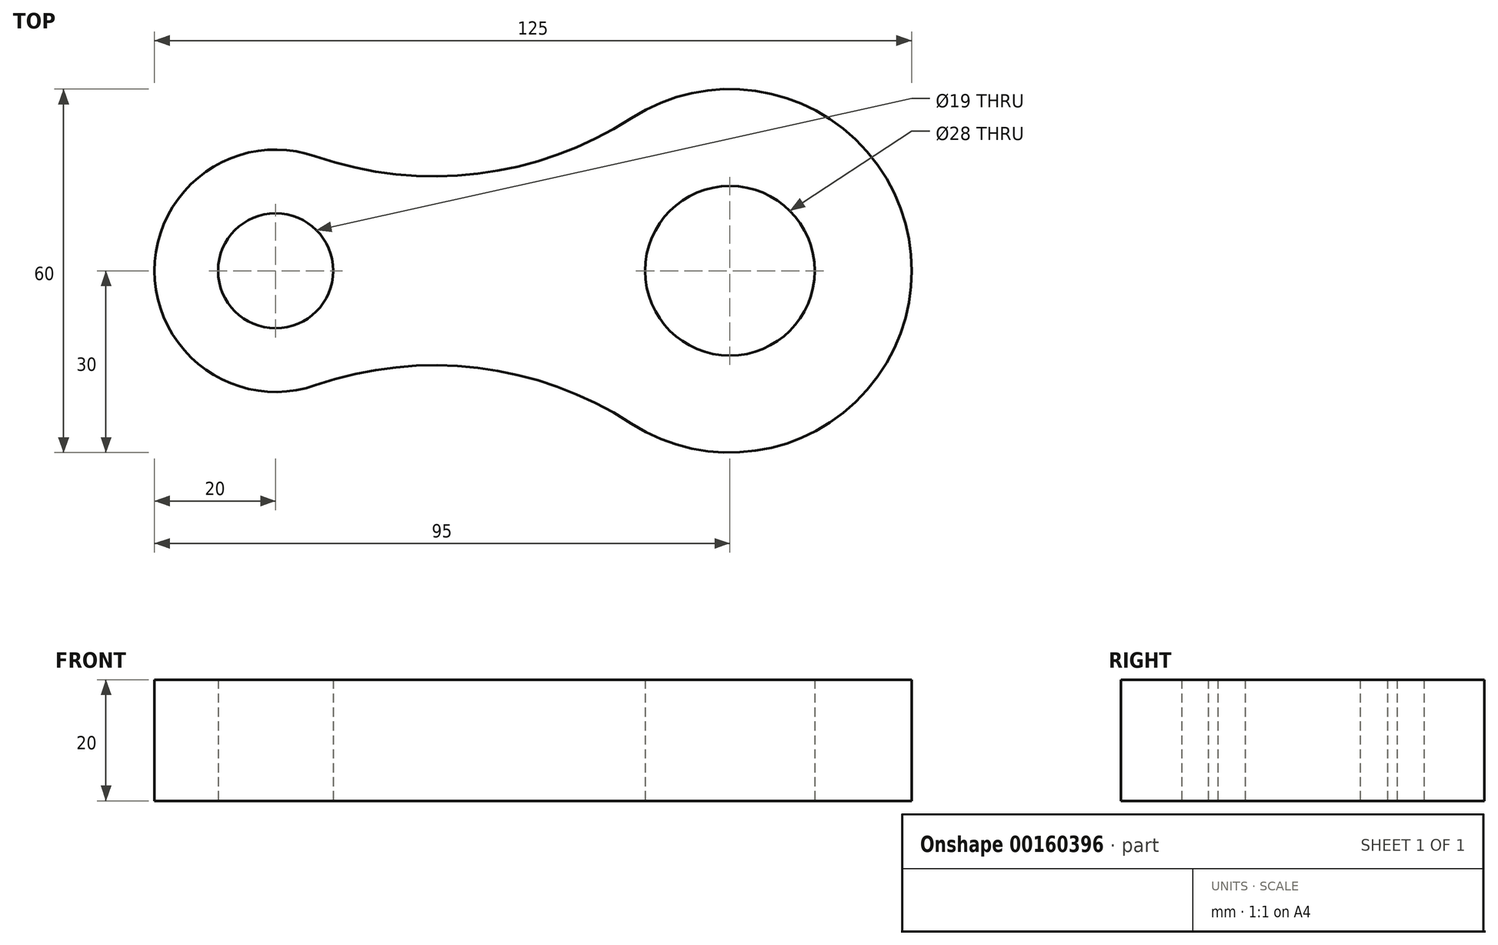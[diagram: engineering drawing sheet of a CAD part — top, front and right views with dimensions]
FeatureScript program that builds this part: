
annotation { "Feature Type Name" : "Feature", "Feature Type Description" : "" }
export const myFeature = defineFeature(function(context is Context, id is Id, definition is map)
    precondition{}
    {
        {
            var Q0;
            Q0=qCreatedBy(makeId("Top.planeOp"),FACE);
            var sketch = newSketch(context, id + "F0", { "sketchPlane" : qUnion([Q0])});
            skCircle(sketch, "E0", {"center": v(0, 0) * mm, "radius": 9.5 * mm});
            skCircle(sketch, "E1", {"center": v(75, 0) * mm, "radius": 14 * mm});
            skArc(sketch, "E2", {"start": v(6.54, 18.9) * mm, "mid": v(-20, 0) * mm, "end": v(6.54, -18.9) * mm});
            skArc(sketch, "E3", {"start": v(58.72, -25.2) * mm, "mid": v(105, 0) * mm, "end": v(58.72, 25.2) * mm});
            skArc(sketch, "E4", {"start": v(58.72, -25.2) * mm, "mid": v(33.36, -16.03) * mm, "end": v(6.54, -18.9) * mm});
            skArc(sketch, "E5", {"start": v(6.54, 18.9) * mm, "mid": v(33.36, 16.03) * mm, "end": v(58.72, 25.2) * mm});
            skSolve(sketch);
        }
        {
            var Q0;
            Q0=makeQuery(id+"F0.imprint","IMPRINT",FACE,{"disambiguationData":[TD([[makeQuery(id+"F0.imprint","IMPRINT",EDGE,{"derivedFrom":sQuery(id+"F0.wireOp",EDGE,"E0")}),-1.0]])]});
            extrude(context, id + "F1", {"entities" : qUnion([Q0]), "depth" : 20 * mm});
        }
    });
